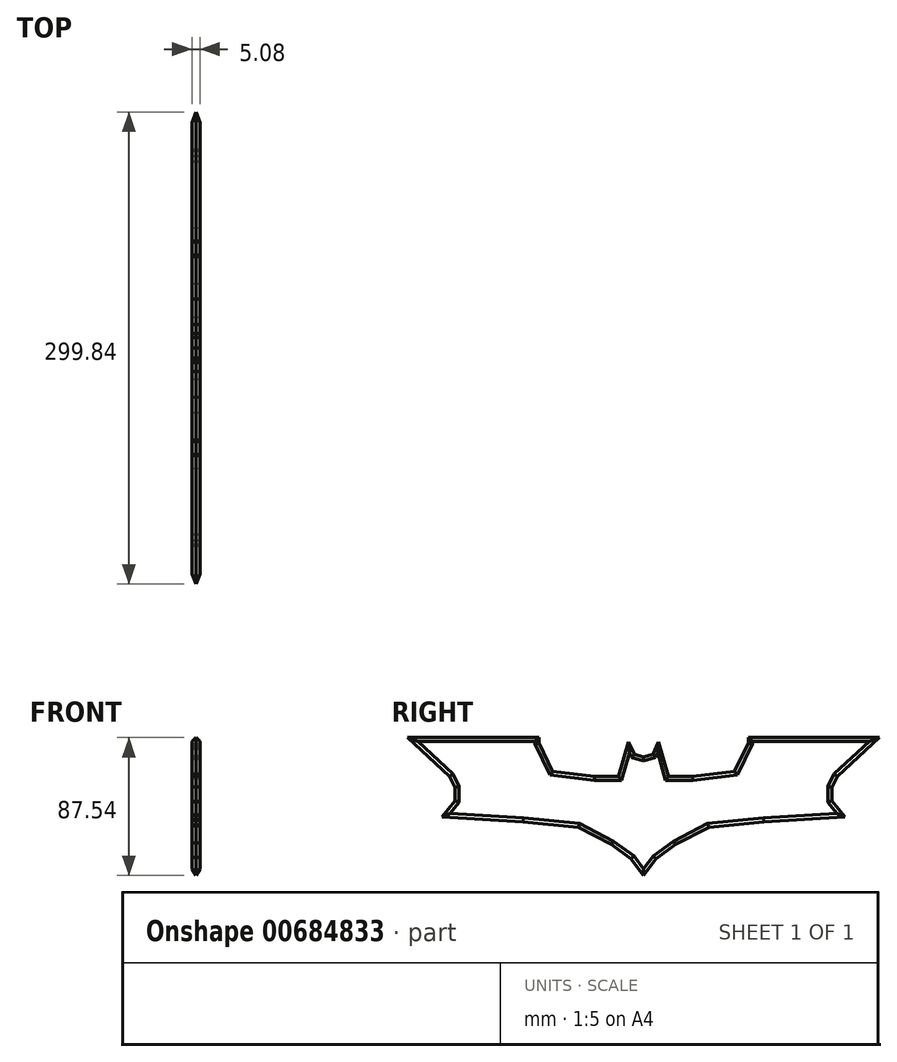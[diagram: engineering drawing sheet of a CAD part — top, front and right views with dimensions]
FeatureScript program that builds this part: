
annotation { "Feature Type Name" : "Feature", "Feature Type Description" : "" }
export const myFeature = defineFeature(function(context is Context, id is Id, definition is map)
    precondition{}
    {
        {
            var Q0;
            Q0=qCreatedBy(makeId("Right.planeOp"),FACE);
            var sketch = newSketch(context, id + "F0", { "sketchPlane" : qUnion([Q0])});
            skLineSegment(sketch, "E0", {"start": v(-149.92, 50.3) * mm, "end": v(-123.14, 25.8) * mm});
            skLineSegment(sketch, "E1", {"start": v(-123.14, 25.8) * mm, "end": v(-119.79, 18.74) * mm});
            skLineSegment(sketch, "E2", {"start": v(-119.79, 18.74) * mm, "end": v(-119.79, 10.22) * mm});
            skLineSegment(sketch, "E3", {"start": v(-119.79, 10.22) * mm, "end": v(-128.02, 0) * mm});
            skLineSegment(sketch, "E4", {"start": v(-20.34, -17.64) * mm, "end": v(-7.94, -26.6) * mm});
            skLineSegment(sketch, "E5", {"start": v(-7.94, -26.6) * mm, "end": v(0, -37.23) * mm});
            skLineSegment(sketch, "E6", {"start": v(-66.49, 50.3) * mm, "end": v(-66.49, 47.05) * mm});
            skLineSegment(sketch, "E7", {"start": v(-66.49, 47.05) * mm, "end": v(-63.02, 39.75) * mm});
            skLineSegment(sketch, "E8", {"start": v(-63.02, 39.75) * mm, "end": v(-57.9, 28.97) * mm});
            skLineSegment(sketch, "E9", {"start": v(-57.9, 28.97) * mm, "end": v(-31.08, 25.8) * mm});
            skLineSegment(sketch, "E10", {"start": v(-31.08, 25.8) * mm, "end": v(-15.97, 25.8) * mm});
            skLineSegment(sketch, "E11", {"start": v(-15.97, 25.8) * mm, "end": v(-9.62, 47.66) * mm});
            skLineSegment(sketch, "E12", {"start": v(-9.62, 47.66) * mm, "end": v(-5.87, 39.78) * mm});
            skLineSegment(sketch, "E13", {"start": v(-5.87, 39.78) * mm, "end": v(0, 38.07) * mm});
            skLineSegment(sketch, "E14.MirrorCS", {"start": v(15.97, 25.8) * mm, "end": v(9.62, 47.66) * mm});
            skLineSegment(sketch, "E15.MirrorCS", {"start": v(57.9, 28.97) * mm, "end": v(31.08, 25.8) * mm});
            skLineSegment(sketch, "E16.MirrorCS", {"start": v(31.08, 25.8) * mm, "end": v(15.97, 25.8) * mm});
            skLineSegment(sketch, "E17.MirrorCS", {"start": v(63.02, 39.75) * mm, "end": v(57.9, 28.97) * mm});
            skLineSegment(sketch, "E18.MirrorCS", {"start": v(66.49, 47.05) * mm, "end": v(63.02, 39.75) * mm});
            skLineSegment(sketch, "E19.MirrorCS", {"start": v(66.49, 50.3) * mm, "end": v(66.49, 47.05) * mm});
            skLineSegment(sketch, "E20.MirrorCS", {"start": v(149.92, 50.3) * mm, "end": v(123.14, 25.8) * mm});
            skLineSegment(sketch, "E21.MirrorCS", {"start": v(123.14, 25.8) * mm, "end": v(119.79, 18.74) * mm});
            skLineSegment(sketch, "E22.MirrorCS", {"start": v(119.79, 18.74) * mm, "end": v(119.79, 10.22) * mm});
            skLineSegment(sketch, "E23.MirrorCS", {"start": v(119.79, 10.22) * mm, "end": v(128.02, 0) * mm});
            skLineSegment(sketch, "E24.MirrorCS", {"start": v(20.34, -17.64) * mm, "end": v(7.94, -26.6) * mm});
            skLineSegment(sketch, "E25.MirrorCS", {"start": v(9.62, 47.66) * mm, "end": v(5.87, 39.78) * mm});
            skLineSegment(sketch, "E26.MirrorCS", {"start": v(5.87, 39.78) * mm, "end": v(0, 38.07) * mm});
            skLineSegment(sketch, "E27.MirrorCS", {"start": v(7.94, -26.6) * mm, "end": v(0, -37.23) * mm});
            skPoint(sketch, "E28.orphan", {"position": v(0, 53.56) * mm});
            skPoint(sketch, "E29.start.orphan", {"position": v(-84.43, -5.83) * mm});
            skPoint(sketch, "E30.start.orphan", {"position": v(-41.46, -11.5) * mm});
            skPoint(sketch, "E31.MirrorCS.end.orphan", {"position": v(20.34, -17.64) * mm});
            skPoint(sketch, "E31.MirrorCS.start.orphan", {"position": v(41.46, -11.5) * mm});
            skPoint(sketch, "E32.MirrorCS.start.orphan", {"position": v(84.43, -5.83) * mm});
            skPoint(sketch, "E33.MirrorCS.start.orphan", {"position": v(128.02, 0) * mm});
            skLineSegment(sketch, "E34", {"start": v(-128.02, 0) * mm, "end": v(-76.48, -3.2) * mm});
            skLineSegment(sketch, "E35", {"start": v(-76.48, -3.2) * mm, "end": v(-41.46, -6.69) * mm});
            skLineSegment(sketch, "E36", {"start": v(-41.46, -6.69) * mm, "end": v(-20.34, -17.64) * mm});
            skLineSegment(sketch, "E37.MirrorCS", {"start": v(128.02, 0) * mm, "end": v(76.48, -3.2) * mm});
            skLineSegment(sketch, "E38.MirrorCS", {"start": v(76.48, -3.2) * mm, "end": v(41.46, -6.69) * mm});
            skLineSegment(sketch, "E39.MirrorCS", {"start": v(41.46, -6.69) * mm, "end": v(20.34, -17.64) * mm});
            skLineSegment(sketch, "E40", {"start": v(-149.92, 50.3) * mm, "end": v(-66.49, 50.3) * mm});
            skPoint(sketch, "E40.startSnap0", {"position": v(-66.49, 50.3) * mm});
            skPoint(sketch, "E41.orphan", {"position": v(-66.49, 53.56) * mm});
            skLineSegment(sketch, "E42.MirrorCS", {"start": v(149.92, 50.3) * mm, "end": v(66.49, 50.3) * mm});
            skPoint(sketch, "E43.MirrorCS.start.orphan", {"position": v(153.48, 53.56) * mm});
            skPoint(sketch, "E44.MirrorCS.end.orphan", {"position": v(66.49, 53.56) * mm});
            skPoint(sketch, "E45.orphan", {"position": v(-153.48, 53.56) * mm});
            skSolve(sketch);
        }
        {
            var Q0;
            Q0 = qSketchRegion(id + "F0", true);
            var Q1;
            {var subQ0=sQuery(id+"F0.wireOp",EDGE,"E1");Q1=makeQuery(id+"F0.imprint","IMPRINT",FACE,{"disambiguationData":[TD([[makeQuery(id+"F0.imprint","IMPRINT",EDGE,{"derivedFrom":subQ0}),1.0]])]});}
            extrude(context, id + "F1", {"entities" : qUnion([Q0, Q1]), "depth" : 5.08 * mm, "offsetDistance" : 25.4 * mm});
        }
        {
            var Q0;
            Q0=makeQuery(id+"F1.opExtrude","CAP_EDGE",EDGE,{"disambiguationData":[OSD([sQuery(id+"F0.wireOp",EDGE,"E40")])],"isStart":false});
            var Q1;
            Q1=makeQuery(id+"F1.opExtrude","CAP_EDGE",EDGE,{"disambiguationData":[OSD([sQuery(id+"F0.wireOp",EDGE,"E0")])],"isStart":false});
            var Q2;
            Q2=makeQuery(id+"F1.opExtrude","CAP_EDGE",EDGE,{"disambiguationData":[OSD([sQuery(id+"F0.wireOp",EDGE,"E1")])],"isStart":false});
            var Q3;
            Q3=makeQuery(id+"F1.opExtrude","CAP_EDGE",EDGE,{"disambiguationData":[OSD([sQuery(id+"F0.wireOp",EDGE,"E2")])],"isStart":false});
            var Q4;
            Q4=makeQuery(id+"F1.opExtrude","CAP_EDGE",EDGE,{"disambiguationData":[OSD([sQuery(id+"F0.wireOp",EDGE,"E3")])],"isStart":false});
            var Q5;
            Q5=makeQuery(id+"F1.opExtrude","CAP_EDGE",EDGE,{"disambiguationData":[OSD([sQuery(id+"F0.wireOp",EDGE,"E36")])],"isStart":false});
            var Q6;
            Q6=makeQuery(id+"F1.opExtrude","CAP_EDGE",EDGE,{"disambiguationData":[OSD([sQuery(id+"F0.wireOp",EDGE,"E9")])],"isStart":false});
            var Q7;
            Q7=makeQuery(id+"F1.opExtrude","CAP_EDGE",EDGE,{"disambiguationData":[OSD([sQuery(id+"F0.wireOp",EDGE,"E10")])],"isStart":false});
            var Q8;
            Q8=makeQuery(id+"F1.opExtrude","CAP_EDGE",EDGE,{"disambiguationData":[OSD([sQuery(id+"F0.wireOp",EDGE,"E11")])],"isStart":false});
            var Q9;
            Q9=makeQuery(id+"F1.opExtrude","CAP_EDGE",EDGE,{"disambiguationData":[OSD([sQuery(id+"F0.wireOp",EDGE,"E12")])],"isStart":false});
            var Q10;
            Q10=makeQuery(id+"F1.opExtrude","CAP_EDGE",EDGE,{"disambiguationData":[OSD([sQuery(id+"F0.wireOp",EDGE,"E13")])],"isStart":false});
            var Q11;
            Q11=makeQuery(id+"F1.opExtrude","CAP_EDGE",EDGE,{"disambiguationData":[OSD([sQuery(id+"F0.wireOp",EDGE,"E26.MirrorCS")])],"isStart":false});
            var Q12;
            Q12=makeQuery(id+"F1.opExtrude","CAP_EDGE",EDGE,{"disambiguationData":[OSD([sQuery(id+"F0.wireOp",EDGE,"E25.MirrorCS")])],"isStart":false});
            var Q13;
            Q13=makeQuery(id+"F1.opExtrude","CAP_EDGE",EDGE,{"disambiguationData":[OSD([sQuery(id+"F0.wireOp",EDGE,"E14.MirrorCS")])],"isStart":false});
            var Q14;
            Q14=makeQuery(id+"F1.opExtrude","CAP_EDGE",EDGE,{"disambiguationData":[OSD([sQuery(id+"F0.wireOp",EDGE,"E15.MirrorCS")])],"isStart":true});
            var Q15;
            Q15=makeQuery(id+"F1.opExtrude","CAP_EDGE",EDGE,{"disambiguationData":[OSD([sQuery(id+"F0.wireOp",EDGE,"E16.MirrorCS")])],"isStart":false});
            var Q16;
            Q16=makeQuery(id+"F1.opExtrude","CAP_FACE",FACE,{"disambiguationData":[OSD([sQuery(id+"F0.wireOp",EDGE,"E0"),sQuery(id+"F0.wireOp",EDGE,"E1"),sQuery(id+"F0.wireOp",EDGE,"E2"),sQuery(id+"F0.wireOp",EDGE,"E3"),sQuery(id+"F0.wireOp",EDGE,"E4"),sQuery(id+"F0.wireOp",EDGE,"E5"),sQuery(id+"F0.wireOp",EDGE,"E6"),sQuery(id+"F0.wireOp",EDGE,"E7"),sQuery(id+"F0.wireOp",EDGE,"E8"),sQuery(id+"F0.wireOp",EDGE,"E9"),sQuery(id+"F0.wireOp",EDGE,"E10"),sQuery(id+"F0.wireOp",EDGE,"E11"),sQuery(id+"F0.wireOp",EDGE,"E12"),sQuery(id+"F0.wireOp",EDGE,"E13"),sQuery(id+"F0.wireOp",EDGE,"E14.MirrorCS"),sQuery(id+"F0.wireOp",EDGE,"E15.MirrorCS"),sQuery(id+"F0.wireOp",EDGE,"E16.MirrorCS"),sQuery(id+"F0.wireOp",EDGE,"E17.MirrorCS"),sQuery(id+"F0.wireOp",EDGE,"E18.MirrorCS"),sQuery(id+"F0.wireOp",EDGE,"E19.MirrorCS"),sQuery(id+"F0.wireOp",EDGE,"E20.MirrorCS"),sQuery(id+"F0.wireOp",EDGE,"E21.MirrorCS"),sQuery(id+"F0.wireOp",EDGE,"E22.MirrorCS"),sQuery(id+"F0.wireOp",EDGE,"E23.MirrorCS"),sQuery(id+"F0.wireOp",EDGE,"E24.MirrorCS"),sQuery(id+"F0.wireOp",EDGE,"E25.MirrorCS"),sQuery(id+"F0.wireOp",EDGE,"E26.MirrorCS"),sQuery(id+"F0.wireOp",EDGE,"E27.MirrorCS"),sQuery(id+"F0.wireOp",EDGE,"E34"),sQuery(id+"F0.wireOp",EDGE,"E35"),sQuery(id+"F0.wireOp",EDGE,"E36"),sQuery(id+"F0.wireOp",EDGE,"E37.MirrorCS"),sQuery(id+"F0.wireOp",EDGE,"E38.MirrorCS"),sQuery(id+"F0.wireOp",EDGE,"E39.MirrorCS"),sQuery(id+"F0.wireOp",EDGE,"E40"),sQuery(id+"F0.wireOp",EDGE,"E42.MirrorCS")])],"isStart":false});
            var Q17;
            Q17=makeQuery(id+"F1.opExtrude","CAP_FACE",FACE,{"disambiguationData":[OSD([sQuery(id+"F0.wireOp",EDGE,"E0"),sQuery(id+"F0.wireOp",EDGE,"E1"),sQuery(id+"F0.wireOp",EDGE,"E2"),sQuery(id+"F0.wireOp",EDGE,"E3"),sQuery(id+"F0.wireOp",EDGE,"E4"),sQuery(id+"F0.wireOp",EDGE,"E5"),sQuery(id+"F0.wireOp",EDGE,"E6"),sQuery(id+"F0.wireOp",EDGE,"E7"),sQuery(id+"F0.wireOp",EDGE,"E8"),sQuery(id+"F0.wireOp",EDGE,"E9"),sQuery(id+"F0.wireOp",EDGE,"E10"),sQuery(id+"F0.wireOp",EDGE,"E11"),sQuery(id+"F0.wireOp",EDGE,"E12"),sQuery(id+"F0.wireOp",EDGE,"E13"),sQuery(id+"F0.wireOp",EDGE,"E14.MirrorCS"),sQuery(id+"F0.wireOp",EDGE,"E15.MirrorCS"),sQuery(id+"F0.wireOp",EDGE,"E16.MirrorCS"),sQuery(id+"F0.wireOp",EDGE,"E17.MirrorCS"),sQuery(id+"F0.wireOp",EDGE,"E18.MirrorCS"),sQuery(id+"F0.wireOp",EDGE,"E19.MirrorCS"),sQuery(id+"F0.wireOp",EDGE,"E20.MirrorCS"),sQuery(id+"F0.wireOp",EDGE,"E21.MirrorCS"),sQuery(id+"F0.wireOp",EDGE,"E22.MirrorCS"),sQuery(id+"F0.wireOp",EDGE,"E23.MirrorCS"),sQuery(id+"F0.wireOp",EDGE,"E24.MirrorCS"),sQuery(id+"F0.wireOp",EDGE,"E25.MirrorCS"),sQuery(id+"F0.wireOp",EDGE,"E26.MirrorCS"),sQuery(id+"F0.wireOp",EDGE,"E27.MirrorCS"),sQuery(id+"F0.wireOp",EDGE,"E34"),sQuery(id+"F0.wireOp",EDGE,"E35"),sQuery(id+"F0.wireOp",EDGE,"E36"),sQuery(id+"F0.wireOp",EDGE,"E37.MirrorCS"),sQuery(id+"F0.wireOp",EDGE,"E38.MirrorCS"),sQuery(id+"F0.wireOp",EDGE,"E39.MirrorCS"),sQuery(id+"F0.wireOp",EDGE,"E40"),sQuery(id+"F0.wireOp",EDGE,"E42.MirrorCS")])],"isStart":true});
            chamfer(context, id + "F2", {"entities" : qUnion([Q0, Q1, Q2, Q3, Q4, Q5, Q6, Q7, Q8, Q9, Q10, Q11, Q12, Q13, Q14, Q15, Q16, Q17]), "width" : 2.54 * mm, "tangentPropagation" : true});
        }
    });
